# Revit family: rba-bim-B35643
name_source: partatom
category: Specialty Equipment
revit_build: Autodesk Revit 2018 (Build: 20170223_1515(x64)
units: mm (PartAtom-declared; Revit-internal decimal feet)

## family parameters
Cut with Voids When Loaded = No
Host = Face
OmniClass Number = 23.40.20.31
OmniClass Title = Refuse Disposal Furniture
Part Type = Normal
Room Calculation Point = No
Round Connector Dimension = Use Diameter
Shared = Yes

## types (1)
- B35643
    ADA Compliant = Yes
    Assembly Code = E1090900
    Default Elevation = 1219 mm
    Description = TrimLineSeries™ Recessed Waste Receptacle
    Height = 1018 mm
    Installation Type = Recessed
    Length = 213 mm
    Manufacturer = Bobrick Washroom Equipment
    Materials and Finishes = Satin Finished Stainless Steel
    Model = B35643
    Modified Issue = 20200422.01
    Price = Prices may vary. Please consult Manufacturer Representative for most up-to-date price list.
    Product Documentation Link = http://bobrick.com
    Product Page URL = http://bobrick.com
    Specification = Recessed waste receptacle shall be Type-304 stainless steel with all-welded construction; exposed surfaces shall have satin fi nish. Door shall be Type-304, 18 gauge (1.2mm) secured to cabinet with a concealed, full-length stainless steel piano-hinge, cable door-swing limiter and equipped with two tumbler locks keyed like other Bobrick washroom accessories. Waste receptacle shall be furnished with a removable, leak-proof, rigid molded plastic waste-container with a minimum capacity of 12-gal. (45.4-L).
    URL = www.rba.com.au
    Warranty Information = 1 Year Limited Warranty
    Width = 440 mm

## geometry (parser evidence)
native form markers: Blend x2, Sweep x3
no freeform markers — native parametric forms only
